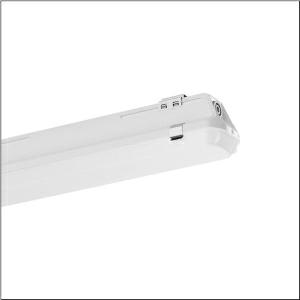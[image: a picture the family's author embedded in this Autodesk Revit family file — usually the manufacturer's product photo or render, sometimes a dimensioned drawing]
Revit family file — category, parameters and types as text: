
# Revit family: monsun_r__11_51fp20mp480h_c015
name_source: partatom
category: Lighting Fixtures
units: mm (PartAtom-declared; Revit-internal decimal feet)

## family parameters
Cut with Voids When Loaded = No
Host = Face
Light Source = No
Part Type = Normal
Room Calculation Point = No
Round Connector Dimension = Use Diameter
Shared = No

## types (1)
- --- (1 x LED, 8220 lm, 52.3 W, 4000K)
    Apparent Load = 52 VA
    CIE Flux Codes = 45 75 93 94 100
    Color Rendering = 80
    Color Temperature = 4000K
    Default Elevation = 1800 mm
    Description = Monsun® 11, damp-proof luminaire, chain hanger, primary optical cover: enclosure, of PC, light emission: direct distribution, primary light characteristic: symmetric, installation type: suspended mounting, surface-mounted, horizontal mounting, vertical mounting, LED, rated luminous flux: 8.220lm, luminous efficacy: 157lm/W, light colour: 840, colour temperature: 4000K, control gear: ECG, with terminal, 3-pole, max. 2.5mm², mains connection: 220..240V, AC, 50/60Hz, rated input power: 52W, luminaire housing, of glass-fibre reinforced polyester, uncoated, bright grey, incl. chain hanger, length: 1.590mm, width: 90mm, height: 88mm, clip for enclosure, of stainless steel (V2A), ceiling mounting element, of stainless steel (V2A), chain hanger, of stainless steel (V2A), protection rating (complete): IP66, insulation class (complete): insulation class I (protective earthing), certification: CE, ENEC, VDE, UKCA, protection symbol: D, impact resistance: IK08, permissible operating ambient temperature: -35..+40°C, standard: EN 50419, EN 60598-2-1, no direct snow, no direct sun, no direct rain, for indoor or canopied outdoor use, corresponds to IFS (International Featured Standards) requirements for safety and quality in the food industry, contact your sales advisor before using the luminaires in applications with unclear chemical exposure, large temperature fluctuations or condensation-forming humidity, LABS conformity tested according to VDMA 24364:2018-05, packaging unit: 1 piece
    Height = 89 mm
    Lamp = 1 x LED
    Lamp Light Flux = 8220 lm
    Lamp Power = 52.3 W
    Lamp count = 1
    Length = 1590 mm
    Luminous efficacy = 157 lm/W
    Manufacturer = Siteco
    ModVariant = No
    Model = 51FP20MP480H
    Mounting Place = Ceiling
    Mounting Type = Surface mounted
    Number of Poles = 1
    OnlyDefault = Yes
    Power Factor = 1
    Product Name = Monsun® 11
    Product group = damp-proof luminaire
    ProductGroupID = 300
    Protection Class = Protection class I
    Protection Degree = IP 66
    RLX_Detail_Level = 1
    RLX_Emergency_Light_Flux = 0 lm
    RLX_Emergency_Type = 0
    RLX_Emergency_Type_DB = No
    RlxData = <blob elided: 89865 chars, md5=18dae592>
    Socket = socket
    Standby Power = 0 W
    System Light Flux = 8220 lm
    System Power = 52 W
    Type Comments = factory setting: luminous flux: 100 % | (A | C | E) | 120 mA
    Type Image = l_1004748.jpg
    URL = http://relux.com
    VarID = @adj_140651
    Voltage = 0 V
    Weight = 0.00 kg
    Width = 90 mm

## geometry (parser evidence)
native form markers: Blend x4, Sweep x15
no freeform markers — native parametric forms only
